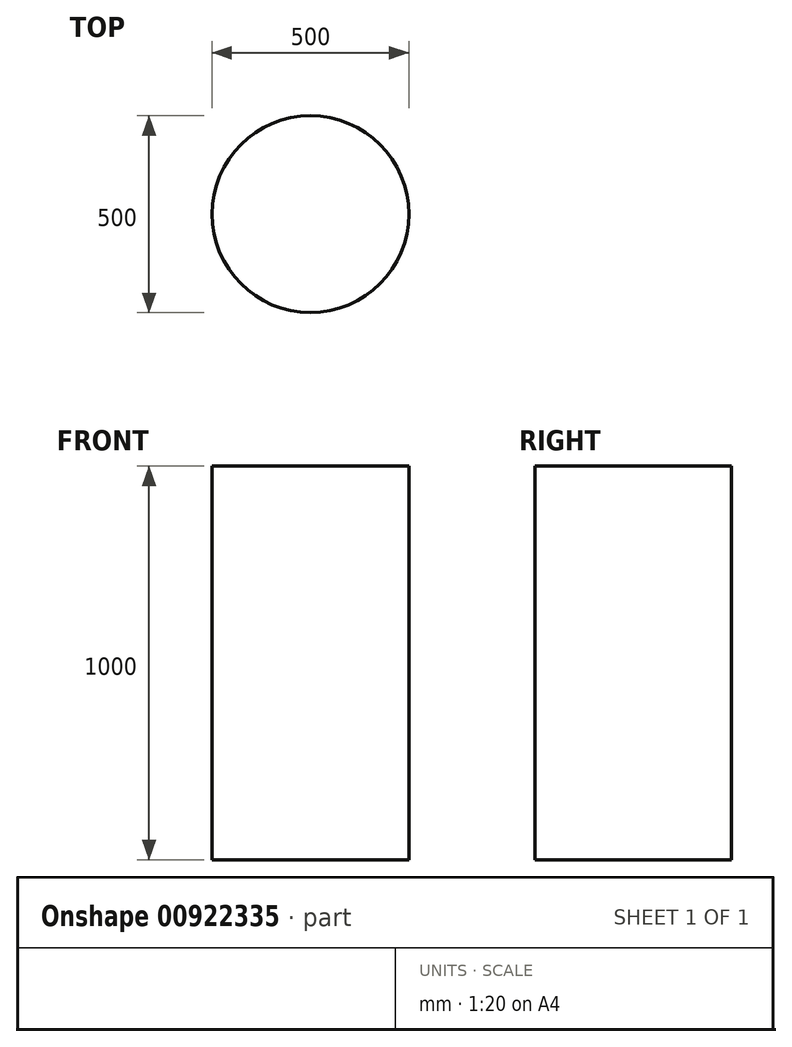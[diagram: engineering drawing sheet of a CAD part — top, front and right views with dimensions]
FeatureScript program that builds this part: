
annotation { "Feature Type Name" : "Feature", "Feature Type Description" : "" }
export const myFeature = defineFeature(function(context is Context, id is Id, definition is map)
    precondition{}
    {
        {
            var Q0;
            Q0=qCreatedBy(makeId("Top.planeOp"),FACE);
            var sketch = newSketch(context, id + "F0", { "sketchPlane" : qUnion([Q0])});
            skCircle(sketch, "E0", {"center": v(0, 0) * mm, "radius": 250 * mm});
            skSolve(sketch);
        }
        {
            var Q0;
            Q0=makeQuery(id+"F0.imprint","IMPRINT",FACE,{"disambiguationData":[TD([[makeQuery(id+"F0.imprint","IMPRINT",EDGE,{"derivedFrom":sQuery(id+"F0.wireOp",EDGE,"E0")}),1.0]])]});
            extrude(context, id + "F1", {"entities" : qUnion([Q0]), "depth" : 1000 * mm, "offsetDistance" : 25 * mm});
        }
    });
